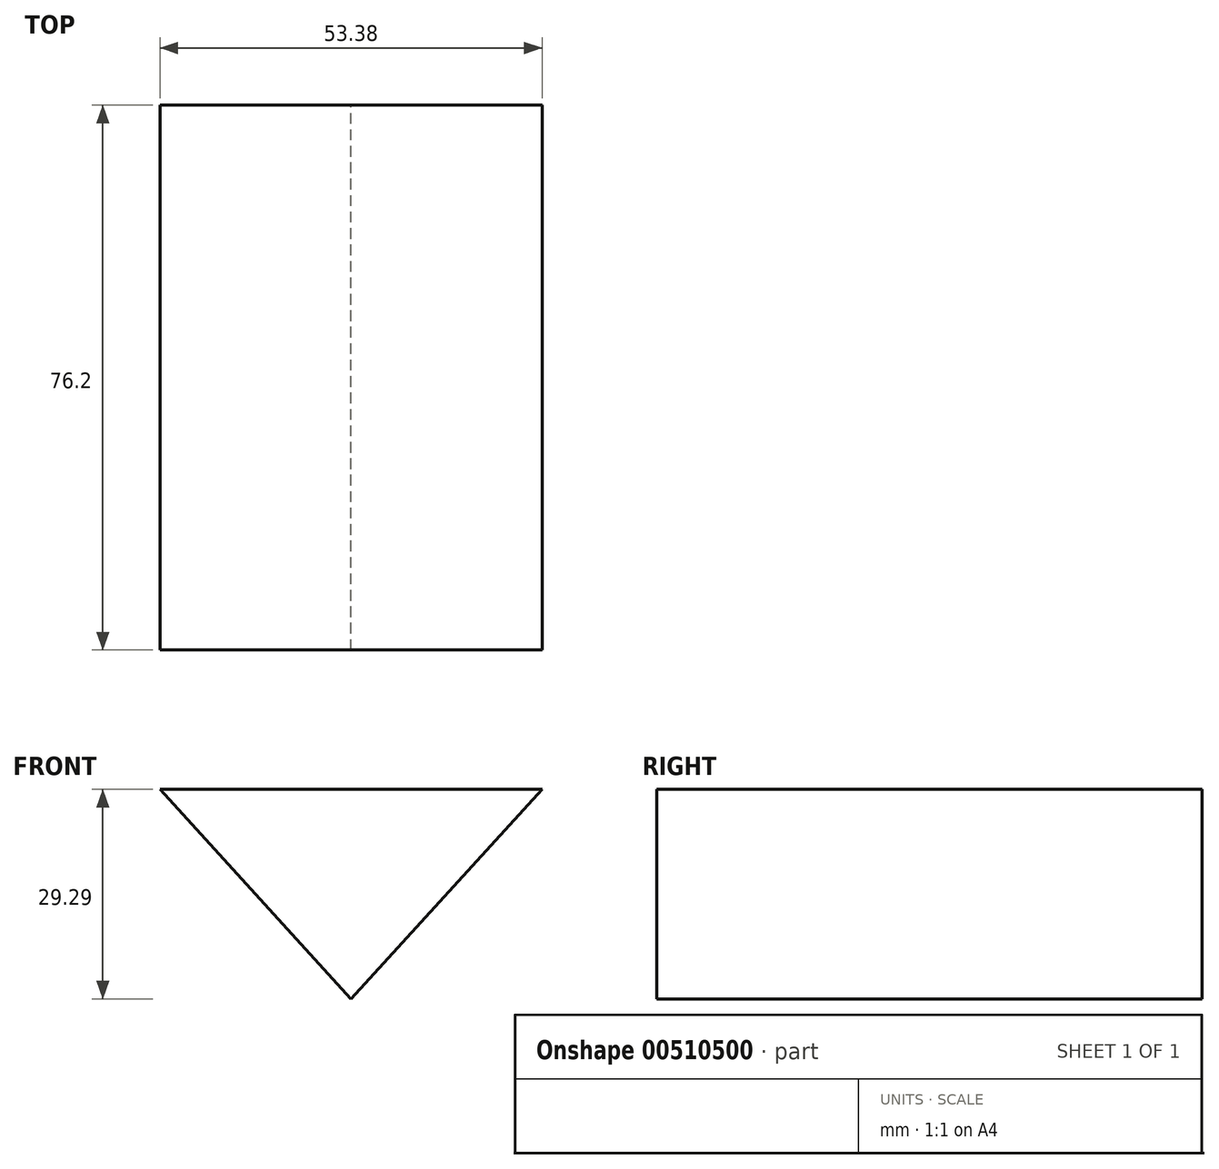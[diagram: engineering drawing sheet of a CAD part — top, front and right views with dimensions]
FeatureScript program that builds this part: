
annotation { "Feature Type Name" : "Feature", "Feature Type Description" : "" }
export const myFeature = defineFeature(function(context is Context, id is Id, definition is map)
    precondition{}
    {
        {
            var Q0;
            Q0=qCreatedBy(makeId("Front.planeOp"),FACE);
            var sketch = newSketch(context, id + "F0", { "sketchPlane" : qUnion([Q0])});
            skLineSegment(sketch, "E0", {"start": v(-26.69, 34.42) * mm, "end": v(26.69, 34.42) * mm});
            skLineSegment(sketch, "E1", {"start": v(-26.69, 34.42) * mm, "end": v(0, 5.13) * mm});
            skLineSegment(sketch, "E2", {"start": v(0, 5.13) * mm, "end": v(26.69, 34.42) * mm});
            skSolve(sketch);
        }
        {
            var Q0;
            Q0 = qSketchRegion(id + "F0", true);
            extrude(context, id + "F1", {"entities" : qUnion([Q0]), "depth" : 76.2 * mm});
        }
    });
